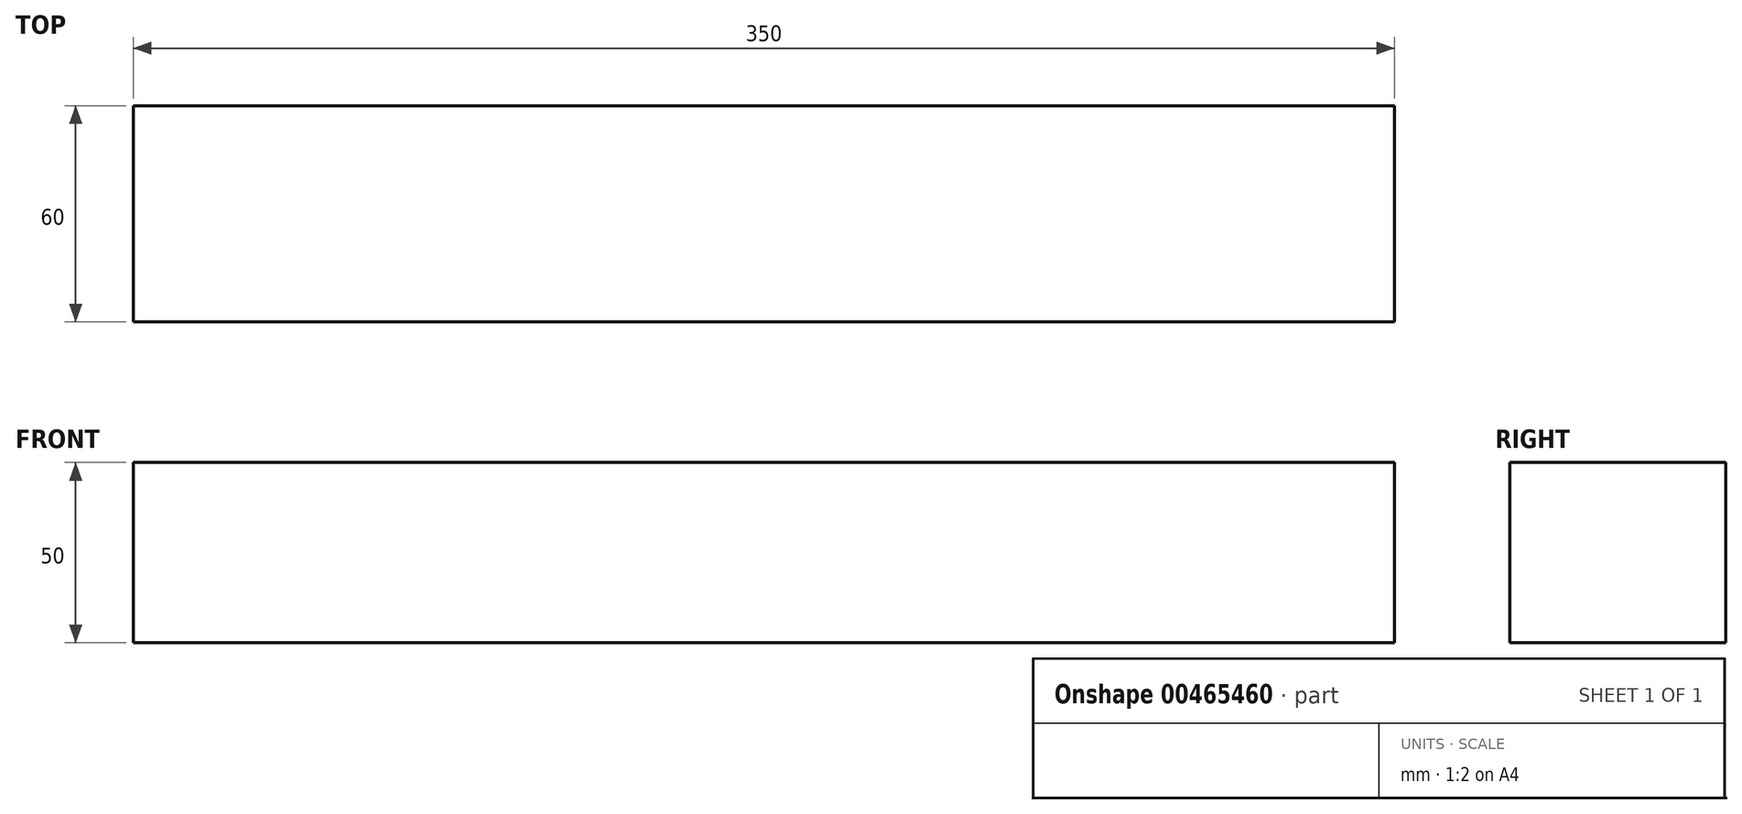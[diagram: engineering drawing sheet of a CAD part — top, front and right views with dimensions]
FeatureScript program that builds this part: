
annotation { "Feature Type Name" : "Feature", "Feature Type Description" : "" }
export const myFeature = defineFeature(function(context is Context, id is Id, definition is map)
    precondition{}
    {
        {
            var Q0;
            Q0=qCreatedBy(makeId("Top.planeOp"),FACE);
            var sketch = newSketch(context, id + "F0", { "sketchPlane" : qUnion([Q0])});
            skLineSegment(sketch, "E0.bottom", {"start": v(-509.87, -280.53) * mm, "end": v(-159.87, -280.53) * mm});
            skLineSegment(sketch, "E0.top", {"start": v(-509.87, -220.53) * mm, "end": v(-159.87, -220.53) * mm});
            skLineSegment(sketch, "E0.left", {"start": v(-509.87, -280.53) * mm, "end": v(-509.87, -220.53) * mm});
            skLineSegment(sketch, "E0.right", {"start": v(-159.87, -280.53) * mm, "end": v(-159.87, -220.53) * mm});
            skSolve(sketch);
        }
        {
            var Q0;
            Q0=qSketchRegion(id+"F0",true);
            extrude(context, id + "F1", {"entities" : qUnion([Q0]), "depth" : 50 * mm});
        }
    });
